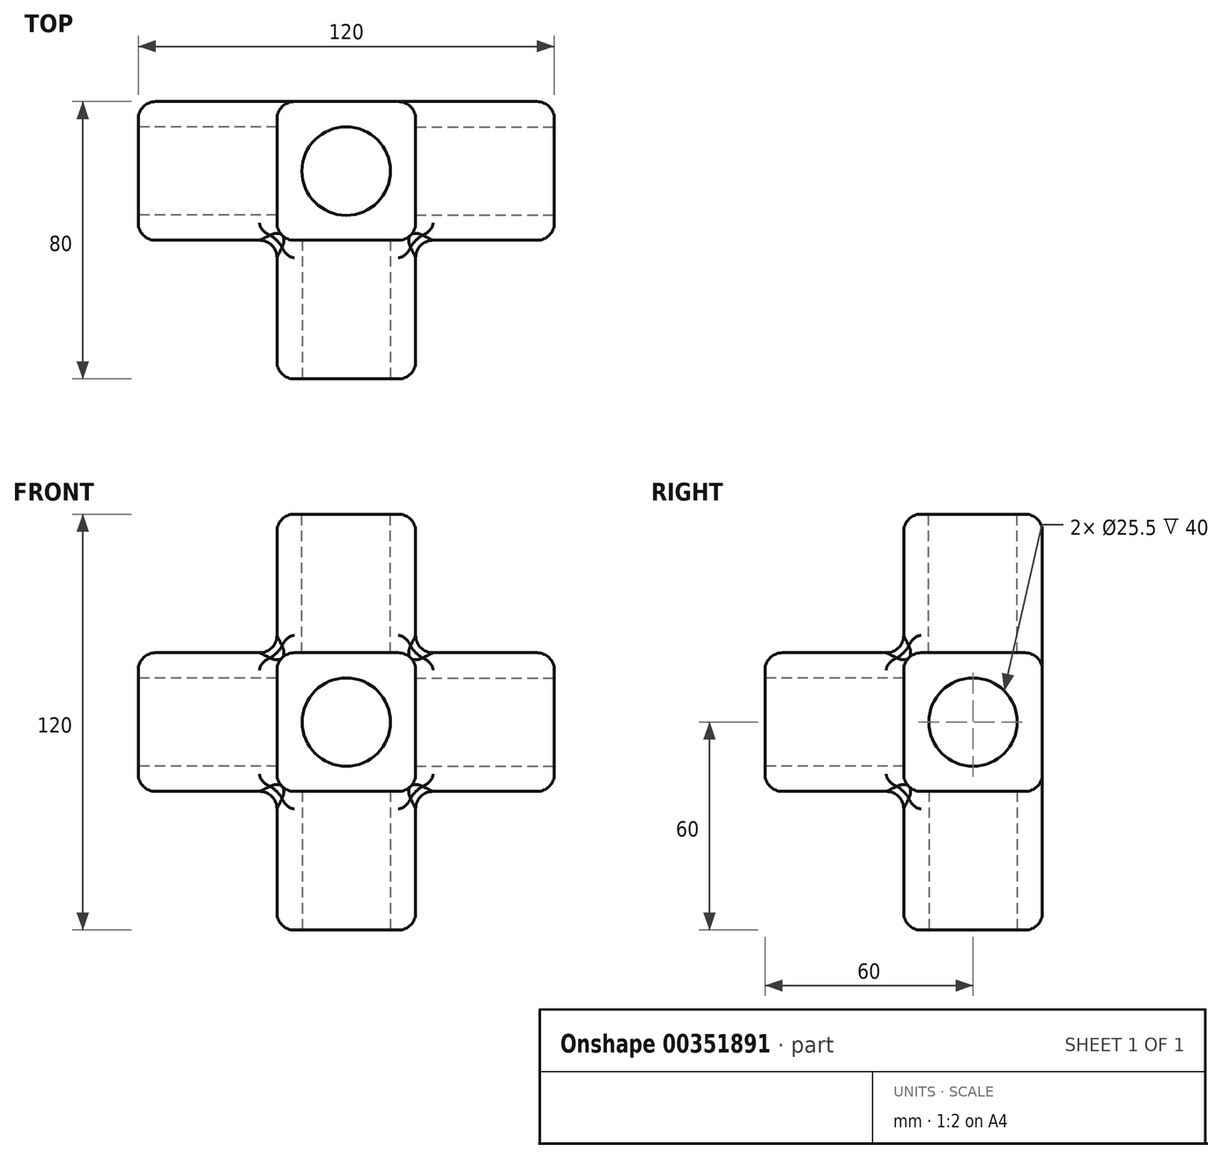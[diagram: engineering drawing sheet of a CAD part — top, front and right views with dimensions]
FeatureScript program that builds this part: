
annotation { "Feature Type Name" : "Feature", "Feature Type Description" : "" }
export const myFeature = defineFeature(function(context is Context, id is Id, definition is map)
    precondition{}
    {
        {
            var Q0;
            Q0=qCreatedBy(makeId("Front.planeOp"),FACE);
            var sketch = newSketch(context, id + "F0", { "sketchPlane" : qUnion([Q0])});
            skLineSegment(sketch, "E0", {"start": v(0, 0) * mm, "end": v(0, 40) * mm});
            skLineSegment(sketch, "E1", {"start": v(0, 40) * mm, "end": v(-40, 40) * mm});
            skLineSegment(sketch, "E2", {"start": v(-40, 40) * mm, "end": v(-40, 80) * mm});
            skLineSegment(sketch, "E3", {"start": v(0, 80) * mm, "end": v(-40, 80) * mm});
            skLineSegment(sketch, "E4", {"start": v(0, 120) * mm, "end": v(0, 80) * mm});
            skLineSegment(sketch, "E5", {"start": v(0, 120) * mm, "end": v(40, 120) * mm});
            skLineSegment(sketch, "E6", {"start": v(40, 120) * mm, "end": v(40, 80) * mm});
            skLineSegment(sketch, "E7", {"start": v(40, 80) * mm, "end": v(80, 80) * mm});
            skLineSegment(sketch, "E8", {"start": v(80, 80) * mm, "end": v(80, 40) * mm});
            skLineSegment(sketch, "E9", {"start": v(80, 40) * mm, "end": v(40, 40) * mm});
            skLineSegment(sketch, "E10", {"start": v(40, 40) * mm, "end": v(40, 0) * mm});
            skLineSegment(sketch, "E11", {"start": v(40, 0) * mm, "end": v(0, 0) * mm});
            skSolve(sketch);
        }
        {
            var Q0;
            Q0=makeQuery(id+"F0.imprint","IMPRINT",FACE,{"disambiguationData":[TD([[makeQuery(id+"F0.imprint","IMPRINT",EDGE,{"derivedFrom":sQuery(id+"F0.wireOp",EDGE,"E0")}),-1.0]])]});
            extrude(context, id + "F1", {"entities" : qUnion([Q0]), "depth" : 40 * mm});
        }
        {
            var Q0;
            Q0=makeQuery(id+"F1.opExtrude","CAP_FACE",FACE,{"disambiguationData":[OSD([sQuery(id+"F0.wireOp",EDGE,"E0"),sQuery(id+"F0.wireOp",EDGE,"E1"),sQuery(id+"F0.wireOp",EDGE,"E2"),sQuery(id+"F0.wireOp",EDGE,"E3"),sQuery(id+"F0.wireOp",EDGE,"E4"),sQuery(id+"F0.wireOp",EDGE,"E5"),sQuery(id+"F0.wireOp",EDGE,"E6"),sQuery(id+"F0.wireOp",EDGE,"E7"),sQuery(id+"F0.wireOp",EDGE,"E8"),sQuery(id+"F0.wireOp",EDGE,"E9"),sQuery(id+"F0.wireOp",EDGE,"E10"),sQuery(id+"F0.wireOp",EDGE,"E11")])],"isStart":false});
            var sketch = newSketch(context, id + "F2", { "sketchPlane" : qUnion([Q0])});
            skLineSegment(sketch, "E12", {"start": v(0, 80) * mm, "end": v(40, 80) * mm});
            skLineSegment(sketch, "E13", {"start": v(40, 80) * mm, "end": v(40, 40) * mm});
            skLineSegment(sketch, "E14", {"start": v(40, 40) * mm, "end": v(0, 40) * mm});
            skLineSegment(sketch, "E15", {"start": v(0, 40) * mm, "end": v(0, 80) * mm});
            skSolve(sketch);
        }
        {
            var Q0;
            Q0=makeQuery(id+"F2.imprint","IMPRINT",FACE,{"disambiguationData":[TD([[makeQuery(id+"F2.imprint","IMPRINT",EDGE,{"derivedFrom":sQuery(id+"F2.wireOp",EDGE,"E12")}),-1.0]])]});
            extrude(context, id + "F3", {"entities" : qUnion([Q0]), "operationType" : NewBodyOperationType.ADD, "depth" : 40 * mm});
        }
        {
            var Q0;
            {var subQ0=sQuery(id+"F0.wireOp",EDGE,"E8");var subQ1=sQuery(id+"F0.wireOp",EDGE,"E7");var subQ2=sQuery(id+"F0.wireOp",EDGE,"E6");var subQ3=sQuery(id+"F0.wireOp",EDGE,"E10");var subQ4=sQuery(id+"F0.wireOp",EDGE,"E9");var subQ5=makeQuery(id+"F1.opExtrude","CAP_FACE",FACE,{"disambiguationData":[OSD([sQuery(id+"F0.wireOp",EDGE,"E0"),sQuery(id+"F0.wireOp",EDGE,"E1"),sQuery(id+"F0.wireOp",EDGE,"E2"),sQuery(id+"F0.wireOp",EDGE,"E3"),sQuery(id+"F0.wireOp",EDGE,"E4"),sQuery(id+"F0.wireOp",EDGE,"E5"),subQ2,subQ1,subQ0,subQ4,subQ3,sQuery(id+"F0.wireOp",EDGE,"E11")])],"isStart":false});Q0=makeQuery(id+"F3.boolean.opBoolean","SPLIT",FACE,{"disambiguationData":[TD([makeQuery(id+"F1.opExtrude","SWEPT_FACE",FACE,{"disambiguationData":[OSD([subQ0])]})])],"derivedFrom":subQ5});}
            var Q1;
            Q1=makeQuery(id+"F1.opExtrude","SWEPT_FACE",FACE,{"disambiguationData":[OSD([sQuery(id+"F0.wireOp",EDGE,"E7")])]});
            var Q2;
            Q2=makeQuery(id+"F1.opExtrude","SWEPT_FACE",FACE,{"disambiguationData":[OSD([sQuery(id+"F0.wireOp",EDGE,"E5")])]});
            var Q3;
            {var subQ0=sQuery(id+"F0.wireOp",EDGE,"E4");var subQ1=sQuery(id+"F0.wireOp",EDGE,"E3");var subQ2=sQuery(id+"F0.wireOp",EDGE,"E5");var subQ3=sQuery(id+"F0.wireOp",EDGE,"E7");var subQ4=sQuery(id+"F0.wireOp",EDGE,"E6");var subQ5=makeQuery(id+"F1.opExtrude","CAP_FACE",FACE,{"disambiguationData":[OSD([sQuery(id+"F0.wireOp",EDGE,"E0"),sQuery(id+"F0.wireOp",EDGE,"E1"),sQuery(id+"F0.wireOp",EDGE,"E2"),subQ1,subQ0,subQ2,subQ4,subQ3,sQuery(id+"F0.wireOp",EDGE,"E8"),sQuery(id+"F0.wireOp",EDGE,"E9"),sQuery(id+"F0.wireOp",EDGE,"E10"),sQuery(id+"F0.wireOp",EDGE,"E11")])],"isStart":false});Q3=makeQuery(id+"F3.boolean.opBoolean","SPLIT",FACE,{"disambiguationData":[TD([makeQuery(id+"F1.opExtrude","SWEPT_FACE",FACE,{"disambiguationData":[OSD([subQ2])]})])],"derivedFrom":subQ5});}
            var Q4;
            Q4=makeQuery(id+"F1.opExtrude","SWEPT_FACE",FACE,{"disambiguationData":[OSD([sQuery(id+"F0.wireOp",EDGE,"E6")])]});
            var Q5;
            Q5=makeQuery(id+"F1.opExtrude","SWEPT_FACE",FACE,{"disambiguationData":[OSD([sQuery(id+"F0.wireOp",EDGE,"E4")])]});
            var Q6;
            Q6=makeQuery(id+"F1.opExtrude","SWEPT_FACE",FACE,{"disambiguationData":[OSD([sQuery(id+"F0.wireOp",EDGE,"E3")])]});
            var Q7;
            Q7=makeQuery(id+"F3.opExtrude","SWEPT_FACE",FACE,{"disambiguationData":[OSD([sQuery(id+"F2.wireOp",EDGE,"E12")])]});
            var Q8;
            Q8=makeQuery(id+"F3.opExtrude","SWEPT_FACE",FACE,{"disambiguationData":[OSD([sQuery(id+"F2.wireOp",EDGE,"E15")])]});
            var Q9;
            Q9=makeQuery(id+"F3.opExtrude","CAP_FACE",FACE,{"disambiguationData":[OSD([sQuery(id+"F2.wireOp",EDGE,"E12"),sQuery(id+"F2.wireOp",EDGE,"E13"),sQuery(id+"F2.wireOp",EDGE,"E14"),sQuery(id+"F2.wireOp",EDGE,"E15")])],"isStart":false});
            var Q10;
            {var subQ0=sQuery(id+"F0.wireOp",EDGE,"E2");var subQ1=sQuery(id+"F0.wireOp",EDGE,"E1");var subQ2=sQuery(id+"F0.wireOp",EDGE,"E4");var subQ3=sQuery(id+"F0.wireOp",EDGE,"E3");var subQ4=sQuery(id+"F0.wireOp",EDGE,"E0");var subQ5=makeQuery(id+"F1.opExtrude","CAP_FACE",FACE,{"disambiguationData":[OSD([subQ4,subQ1,subQ0,subQ3,subQ2,sQuery(id+"F0.wireOp",EDGE,"E5"),sQuery(id+"F0.wireOp",EDGE,"E6"),sQuery(id+"F0.wireOp",EDGE,"E7"),sQuery(id+"F0.wireOp",EDGE,"E8"),sQuery(id+"F0.wireOp",EDGE,"E9"),sQuery(id+"F0.wireOp",EDGE,"E10"),sQuery(id+"F0.wireOp",EDGE,"E11")])],"isStart":false});Q10=makeQuery(id+"F3.boolean.opBoolean","SPLIT",FACE,{"disambiguationData":[TD([makeQuery(id+"F1.opExtrude","SWEPT_FACE",FACE,{"disambiguationData":[OSD([subQ0])]})])],"derivedFrom":subQ5});}
            var Q11;
            Q11=makeQuery(id+"F1.opExtrude","SWEPT_FACE",FACE,{"disambiguationData":[OSD([sQuery(id+"F0.wireOp",EDGE,"E2")])]});
            var Q12;
            Q12=makeQuery(id+"F1.opExtrude","SWEPT_FACE",FACE,{"disambiguationData":[OSD([sQuery(id+"F0.wireOp",EDGE,"E1")])]});
            var Q13;
            Q13=makeQuery(id+"F1.opExtrude","SWEPT_FACE",FACE,{"disambiguationData":[OSD([sQuery(id+"F0.wireOp",EDGE,"E0")])]});
            var Q14;
            Q14=makeQuery(id+"F1.opExtrude","SWEPT_FACE",FACE,{"disambiguationData":[OSD([sQuery(id+"F0.wireOp",EDGE,"E11")])]});
            var Q15;
            {var subQ0=sQuery(id+"F0.wireOp",EDGE,"E9");var subQ1=sQuery(id+"F0.wireOp",EDGE,"E0");var subQ2=sQuery(id+"F0.wireOp",EDGE,"E1");var subQ3=sQuery(id+"F0.wireOp",EDGE,"E11");var subQ4=sQuery(id+"F0.wireOp",EDGE,"E10");var subQ5=makeQuery(id+"F1.opExtrude","CAP_FACE",FACE,{"disambiguationData":[OSD([subQ1,subQ2,sQuery(id+"F0.wireOp",EDGE,"E2"),sQuery(id+"F0.wireOp",EDGE,"E3"),sQuery(id+"F0.wireOp",EDGE,"E4"),sQuery(id+"F0.wireOp",EDGE,"E5"),sQuery(id+"F0.wireOp",EDGE,"E6"),sQuery(id+"F0.wireOp",EDGE,"E7"),sQuery(id+"F0.wireOp",EDGE,"E8"),subQ0,subQ4,subQ3])],"isStart":false});Q15=makeQuery(id+"F3.boolean.opBoolean","SPLIT",FACE,{"disambiguationData":[TD([makeQuery(id+"F1.opExtrude","SWEPT_FACE",FACE,{"disambiguationData":[OSD([subQ3])]})])],"derivedFrom":subQ5});}
            var Q16;
            Q16=makeQuery(id+"F3.opExtrude","SWEPT_FACE",FACE,{"disambiguationData":[OSD([sQuery(id+"F2.wireOp",EDGE,"E14")])]});
            var Q17;
            Q17=makeQuery(id+"F1.opExtrude","SWEPT_FACE",FACE,{"disambiguationData":[OSD([sQuery(id+"F0.wireOp",EDGE,"E10")])]});
            var Q18;
            Q18=makeQuery(id+"F3.opExtrude","SWEPT_FACE",FACE,{"disambiguationData":[OSD([sQuery(id+"F2.wireOp",EDGE,"E13")])]});
            var Q19;
            Q19=makeQuery(id+"F1.opExtrude","SWEPT_FACE",FACE,{"disambiguationData":[OSD([sQuery(id+"F0.wireOp",EDGE,"E9")])]});
            var Q20;
            Q20=makeQuery(id+"F1.opExtrude","SWEPT_FACE",FACE,{"disambiguationData":[OSD([sQuery(id+"F0.wireOp",EDGE,"E8")])]});
            var Q21;
            Q21=makeQuery(id+"F1.opExtrude","CAP_FACE",FACE,{"disambiguationData":[OSD([sQuery(id+"F0.wireOp",EDGE,"E0"),sQuery(id+"F0.wireOp",EDGE,"E1"),sQuery(id+"F0.wireOp",EDGE,"E2"),sQuery(id+"F0.wireOp",EDGE,"E3"),sQuery(id+"F0.wireOp",EDGE,"E4"),sQuery(id+"F0.wireOp",EDGE,"E5"),sQuery(id+"F0.wireOp",EDGE,"E6"),sQuery(id+"F0.wireOp",EDGE,"E7"),sQuery(id+"F0.wireOp",EDGE,"E8"),sQuery(id+"F0.wireOp",EDGE,"E9"),sQuery(id+"F0.wireOp",EDGE,"E10"),sQuery(id+"F0.wireOp",EDGE,"E11")])],"isStart":true});
            fillet(context, id + "F4", {"entities" : qUnion([Q0, Q1, Q2, Q3, Q4, Q5, Q6, Q7, Q8, Q9, Q10, Q11, Q12, Q13, Q14, Q15, Q16, Q17, Q18, Q19, Q20, Q21]), "radius" : 5 * mm, "tangentPropagation" : true, "allowEdgeOverflow" : false});
        }
        {
            var Q0;
            Q0=makeQuery(id+"F3.opExtrude","CAP_FACE",FACE,{"disambiguationData":[OSD([sQuery(id+"F2.wireOp",EDGE,"E12"),sQuery(id+"F2.wireOp",EDGE,"E13"),sQuery(id+"F2.wireOp",EDGE,"E14"),sQuery(id+"F2.wireOp",EDGE,"E15")])],"isStart":false});
            var sketch = newSketch(context, id + "F5", { "sketchPlane" : qUnion([Q0])});
            skLineSegment(sketch, "E16", {"start": v(5, 45) * mm, "end": v(35, 75) * mm, "construction": true});
            skLineSegment(sketch, "E17", {"start": v(5, 75) * mm, "end": v(35, 45) * mm, "construction": true});
            skCircle(sketch, "E18", {"center": v(20, 60) * mm, "radius": 12.75 * mm});
            skSolve(sketch);
        }
        {
            var Q0;
            Q0 = qSketchRegion(id + "F5", true);
            extrude(context, id + "F6", {"entities" : qUnion([Q0]), "operationType" : NewBodyOperationType.REMOVE, "oppositeDirection" : true, "depth" : 40 * mm});
        }
        {
            var Q0;
            Q0=makeQuery(id+"F1.opExtrude","SWEPT_FACE",FACE,{"disambiguationData":[OSD([sQuery(id+"F0.wireOp",EDGE,"E11")])]});
            var sketch = newSketch(context, id + "F7", { "sketchPlane" : qUnion([Q0])});
            skLineSegment(sketch, "E19", {"start": v(5, 5) * mm, "end": v(35, 35) * mm});
            skLineSegment(sketch, "E20", {"start": v(35, 35) * mm, "end": v(5, 35) * mm, "construction": true});
            skLineSegment(sketch, "E21", {"start": v(5, 35) * mm, "end": v(35, 5) * mm, "construction": true});
            skCircle(sketch, "E22", {"center": v(20, 20) * mm, "radius": 12.75 * mm});
            skSolve(sketch);
        }
        {
            var Q0;
            Q0 = qSketchRegion(id + "F7", true);
            extrude(context, id + "F8", {"entities" : qUnion([Q0]), "operationType" : NewBodyOperationType.REMOVE, "oppositeDirection" : true, "depth" : 40 * mm});
        }
        {
            var Q0;
            Q0=makeQuery(id+"F1.opExtrude","SWEPT_FACE",FACE,{"disambiguationData":[OSD([sQuery(id+"F0.wireOp",EDGE,"E2")])]});
            var sketch = newSketch(context, id + "F9", { "sketchPlane" : qUnion([Q0])});
            skLineSegment(sketch, "E23", {"start": v(5, 45) * mm, "end": v(35, 75) * mm, "construction": true});
            skLineSegment(sketch, "E24", {"start": v(35, 75) * mm, "end": v(5, 75) * mm, "construction": true});
            skLineSegment(sketch, "E25", {"start": v(5, 75) * mm, "end": v(35, 45) * mm, "construction": true});
            skCircle(sketch, "E26", {"center": v(20, 60) * mm, "radius": 12.75 * mm});
            skSolve(sketch);
        }
        {
            var Q0;
            Q0=makeQuery(id+"F9.imprint","IMPRINT",FACE,{"disambiguationData":[TD([[makeQuery(id+"F9.imprint","IMPRINT",EDGE,{"derivedFrom":sQuery(id+"F9.wireOp",EDGE,"E26")}),1.0]])]});
            extrude(context, id + "F10", {"entities" : qUnion([Q0]), "operationType" : NewBodyOperationType.REMOVE, "oppositeDirection" : true, "depth" : 40 * mm});
        }
        {
            var Q0;
            Q0=makeQuery(id+"F1.opExtrude","SWEPT_FACE",FACE,{"disambiguationData":[OSD([sQuery(id+"F0.wireOp",EDGE,"E5")])]});
            var sketch = newSketch(context, id + "F11", { "sketchPlane" : qUnion([Q0])});
            skLineSegment(sketch, "E27", {"start": v(5, -35) * mm, "end": v(35, -5) * mm, "construction": true});
            skLineSegment(sketch, "E28", {"start": v(35, -5) * mm, "end": v(5, -5) * mm, "construction": true});
            skLineSegment(sketch, "E29", {"start": v(5, -5) * mm, "end": v(34.92, -35.06) * mm, "construction": true});
            skCircle(sketch, "E30", {"center": v(19.96, -20.03) * mm, "radius": 12.75 * mm});
            skSolve(sketch);
        }
        {
            var Q0;
            Q0=makeQuery(id+"F11.imprint","IMPRINT",FACE,{"disambiguationData":[TD([[makeQuery(id+"F11.imprint","IMPRINT",EDGE,{"derivedFrom":sQuery(id+"F11.wireOp",EDGE,"E30")}),1.0]])]});
            var Q1;
            Q1=sQuery(id+"F11.wireOp",EDGE,"E30");
            extrude(context, id + "F12", {"entities" : qUnion([Q0]), "operationType" : NewBodyOperationType.REMOVE, "surfaceEntities" : qUnion([Q1]), "oppositeDirection" : true, "depth" : 40 * mm});
        }
        {
            var Q0;
            Q0=makeQuery(id+"F1.opExtrude","SWEPT_FACE",FACE,{"disambiguationData":[OSD([sQuery(id+"F0.wireOp",EDGE,"E8")])]});
            var sketch = newSketch(context, id + "F13", { "sketchPlane" : qUnion([Q0])});
            skLineSegment(sketch, "E31", {"start": v(-35, 45) * mm, "end": v(-5, 75) * mm, "construction": true});
            skLineSegment(sketch, "E32", {"start": v(-5, 75) * mm, "end": v(-35, 75) * mm, "construction": true});
            skLineSegment(sketch, "E33", {"start": v(-35, 75) * mm, "end": v(-5, 45) * mm, "construction": true});
            skCircle(sketch, "E34", {"center": v(-20, 60) * mm, "radius": 12.75 * mm});
            skSolve(sketch);
        }
        {
            var Q0;
            Q0 = qSketchRegion(id + "F13", true);
            extrude(context, id + "F14", {"entities" : qUnion([Q0]), "operationType" : NewBodyOperationType.REMOVE, "oppositeDirection" : true, "depth" : 40 * mm});
        }
    });
